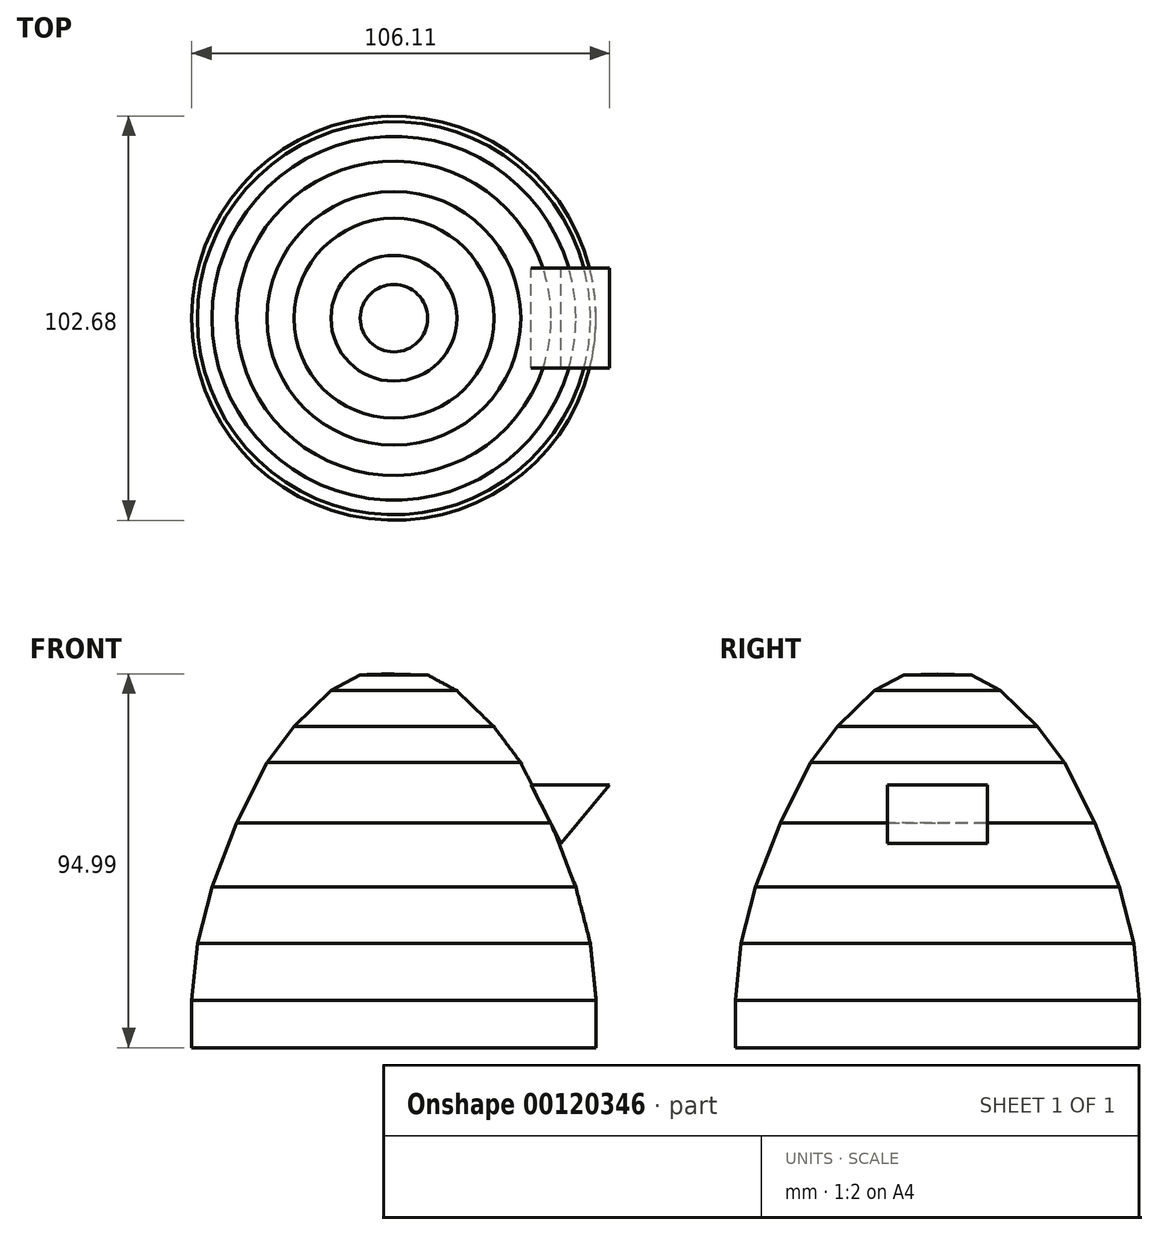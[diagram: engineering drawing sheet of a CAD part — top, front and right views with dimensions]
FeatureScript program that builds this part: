
annotation { "Feature Type Name" : "Feature", "Feature Type Description" : "" }
export const myFeature = defineFeature(function(context is Context, id is Id, definition is map)
    precondition{}
    {
        {
            var Q0;
            Q0=qCreatedBy(makeId("Front.planeOp"),FACE);
            var sketch = newSketch(context, id + "F0", { "sketchPlane" : qUnion([Q0])});
            skLineSegment(sketch, "E0", {"start": v(0, 46.07) * mm, "end": v(0, -48.92) * mm});
            skLineSegment(sketch, "E1", {"start": v(0, -48.92) * mm, "end": v(51.34, -48.92) * mm});
            skLineSegment(sketch, "E2", {"start": v(51.34, -48.92) * mm, "end": v(51.34, -36.94) * mm});
            skLineSegment(sketch, "E3", {"start": v(51.34, -36.94) * mm, "end": v(49.92, -22.4) * mm});
            skLineSegment(sketch, "E4", {"start": v(49.92, -22.4) * mm, "end": v(46.2, -8.13) * mm});
            skLineSegment(sketch, "E5", {"start": v(46.2, -8.13) * mm, "end": v(39.93, 8.13) * mm});
            skLineSegment(sketch, "E6", {"start": v(39.93, 8.13) * mm, "end": v(32.23, 23.53) * mm});
            skLineSegment(sketch, "E7", {"start": v(32.23, 23.53) * mm, "end": v(25.39, 32.66) * mm});
            skLineSegment(sketch, "E8", {"start": v(25.39, 32.66) * mm, "end": v(15.97, 41.79) * mm});
            skLineSegment(sketch, "E9", {"start": v(15.97, 41.79) * mm, "end": v(8.56, 45.78) * mm});
            skLineSegment(sketch, "E10", {"start": v(8.56, 45.78) * mm, "end": v(0, 46.07) * mm});
            skSolve(sketch);
        }
        {
            var Q0;
            Q0=makeQuery(id+"F0.imprint","IMPRINT",FACE,{"disambiguationData":[TD([[makeQuery(id+"F0.imprint","IMPRINT",EDGE,{"derivedFrom":sQuery(id+"F0.wireOp",EDGE,"E0")}),1.0]])]});
            var Q1;
            Q1=sQuery(id+"F0.wireOp",EDGE,"E0");
            revolve(context, id + "F1", {"entities" : qUnion([Q0]), "axis" : qUnion([Q1]), "revolveType" : RevolveType.FULL});
        }
        {
            var Q0;
            Q0=qCreatedBy(makeId("Front.planeOp"),FACE);
            var sketch = newSketch(context, id + "F2", { "sketchPlane" : qUnion([Q0])});
            skLineSegment(sketch, "E11", {"start": v(34.8, 17.83) * mm, "end": v(54.77, 17.83) * mm});
            skLineSegment(sketch, "E12", {"start": v(54.77, 17.83) * mm, "end": v(42.5, 3) * mm});
            skLineSegment(sketch, "E13", {"start": v(42.5, 3) * mm, "end": v(34.8, 17.83) * mm});
            skSolve(sketch);
        }
        {
            var Q0;
            Q0 = qSketchRegion(id + "F2", true);
            extrude(context, id + "F3", {"entities" : qUnion([Q0]), "endBound" : BoundingType.SYMMETRIC, "depth" : 25.4 * mm});
        }
        {
            var Q0;
            Q0 = qConstructionFilter(qBodyType(qCreatedBy(id + "F2" ,EDGE), BodyType.WIRE), ConstructionObject.NO);
            extrude(context, id + "F4", {"bodyType" : ToolBodyType.SURFACE, "surfaceEntities" : qUnion([Q0]), "depth" : 25.4 * mm});
        }
        {
            var Q0;
            Q0=makeQuery(id+"F3.opExtrude","SWEPT_BODY",BODY,{"disambiguationData":[OSD([sQuery(id+"F2.wireOp",EDGE,"E11"),sQuery(id+"F2.wireOp",EDGE,"E12"),sQuery(id+"F2.wireOp",EDGE,"E13")])]});
            transform(context, id + "F5", {"entities" : qUnion([Q0]), "transformType" : TransformType.TRANSLATION_3D, "dx" : 0 * mm, "dy" : 0 * mm, "dz" : 0 * mm, "makeCopy" : false});
        }
    });
